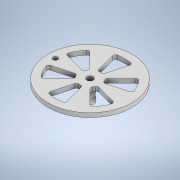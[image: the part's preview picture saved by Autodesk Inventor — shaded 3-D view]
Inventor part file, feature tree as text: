
AUTODESK INVENTOR PART (.ipt)
format: ipt  version: 2020 (Build 240168000, 168)  size: 230,400 bytes
history: native  units: in
note: dims shown in document units (in); Inventor stores cm internally (conversion verified against a paired STEP export)
features: extrude x5, sketch x5
ambient origin geometry x8: Origin, YZ Plane, XZ Plane, XY Plane, X Axis, Y Axis, Z Axis, Center Point
bodies: Solid1 (feature_tree)
feature tree (10):
  extrude  "Extrusion1"  Depth=0.5906in TaperAngle=0.0deg
  extrude  "Extrusion2"  Depth=0.5118in TaperAngle=0.0deg
  extrude  "Extrusion3"  Depth=0.1575in
  extrude  "Extrusion8"  Depth=3.1496in
  extrude  "Extrusion9"  TaperAngle=0.0deg  [1 undecoded]
  sketch  "Sketch1"  dims[d0=0.315in d1=0.5906in d2=0.0in]
  sketch  "Sketch2"  dims[d3=0.2362in d4=0.5118in d5=0.0in]
  sketch  "Sketch3"  dims[d8=0.1575in d9=0.1575in]
  sketch  "Sketch9"  dims[d10=0.9843in d11=0.0in d47=3.1496in]
  sketch  "Sketch10"  dims[d48=0.1575in d49=0.0in d50=0.0in d51=0.0in d54=0.1772in d58=15.0deg d60=30.0deg d61=0.7874in d62=0.0787in d63=0.0787in d64=2.3622in d66=360.0deg]
note: 1 required parameter value undecoded (feature->parameter linkage not recoverable at this tier; creation-order binding heuristic only, values carry confidence <= 0.55)
